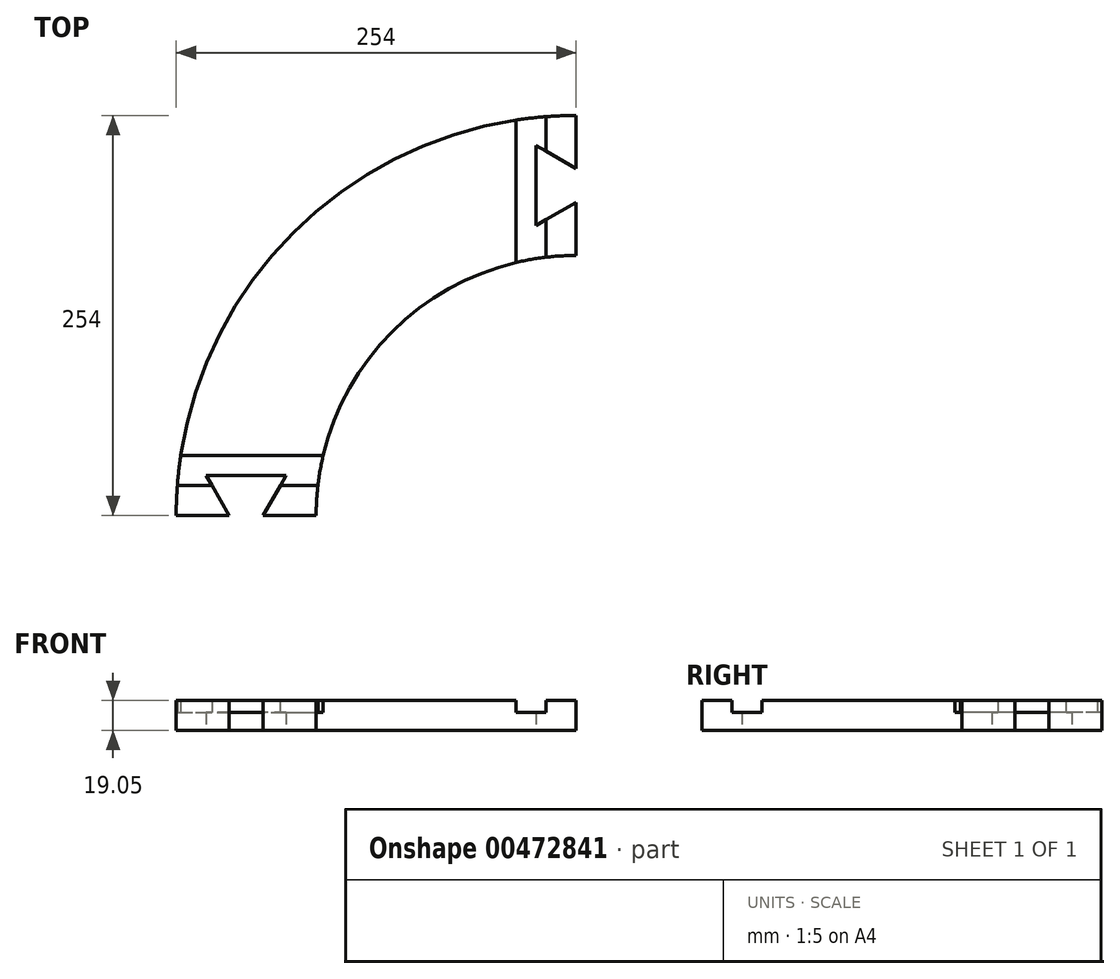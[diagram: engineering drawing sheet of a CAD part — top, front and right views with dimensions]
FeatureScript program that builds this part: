
annotation { "Feature Type Name" : "Feature", "Feature Type Description" : "" }
export const myFeature = defineFeature(function(context is Context, id is Id, definition is map)
    precondition{}
    {
        {
            var Q0;
            Q0=qCreatedBy(makeId("Top.planeOp"),FACE);
            var sketch = newSketch(context, id + "F0", { "sketchPlane" : qUnion([Q0])});
            skArc(sketch, "E0", {"start": v(-254, 0) * mm, "mid": v(-179.6, 179.6) * mm, "end": v(0, 254) * mm});
            skArc(sketch, "E1.0", {"start": v(-165.1, 0) * mm, "mid": v(-116.74, 116.74) * mm, "end": v(0, 165.1) * mm});
            skLineSegment(sketch, "E2", {"start": v(-254, 0) * mm, "end": v(-220.29, 0) * mm});
            skLineSegment(sketch, "E3", {"start": v(0, 254) * mm, "end": v(0, 220.29) * mm});
            skLineSegment(sketch, "E4", {"start": v(-220.29, 0) * mm, "end": v(-234.95, 25.4) * mm});
            skLineSegment(sketch, "E5", {"start": v(-234.95, 25.4) * mm, "end": v(-184.15, 25.4) * mm});
            skLineSegment(sketch, "E6", {"start": v(-184.15, 25.4) * mm, "end": v(-198.81, 0) * mm});
            skLineSegment(sketch, "E7.trimOffspring", {"start": v(-198.81, 0) * mm, "end": v(-165.1, 0) * mm});
            skLineSegment(sketch, "E8", {"start": v(0, 220.29) * mm, "end": v(-25.4, 234.95) * mm});
            skLineSegment(sketch, "E9", {"start": v(-25.4, 234.95) * mm, "end": v(-25.4, 184.15) * mm});
            skLineSegment(sketch, "E10", {"start": v(-25.4, 184.15) * mm, "end": v(0, 198.81) * mm});
            skLineSegment(sketch, "E11.trimOffspring", {"start": v(0, 198.81) * mm, "end": v(0, 165.1) * mm});
            skSolve(sketch);
        }
        {
            var Q0;
            Q0=qSketchRegion(id+"F0",true);
            extrude(context, id + "F1", {"entities" : qUnion([Q0]), "depth" : 19.05 * mm});
        }
        {
            var Q0;
            Q0=qCreatedBy(makeId("Right.planeOp"),FACE);
            var sketch = newSketch(context, id + "F2", { "sketchPlane" : qUnion([Q0])});
            skLineSegment(sketch, "E12.bottom", {"start": v(19.05, 11.43) * mm, "end": v(38.1, 11.43) * mm});
            skLineSegment(sketch, "E12.top", {"start": v(19.05, 19.05) * mm, "end": v(38.1, 19.05) * mm});
            skLineSegment(sketch, "E12.left", {"start": v(19.05, 11.43) * mm, "end": v(19.05, 19.05) * mm});
            skLineSegment(sketch, "E12.right", {"start": v(38.1, 11.43) * mm, "end": v(38.1, 19.05) * mm});
            skSolve(sketch);
        }
        {
            var Q0;
            Q0=qSketchRegion(id+"F2",true);
            extrude(context, id + "F3", {"entities" : qUnion([Q0]), "operationType" : NewBodyOperationType.REMOVE, "endBound" : BoundingType.THROUGH_ALL, "oppositeDirection" : true, "depth" : 25.4 * mm});
        }
        {
            var Q0;
            Q0=qCreatedBy(makeId("Front.planeOp"),FACE);
            var sketch = newSketch(context, id + "F4", { "sketchPlane" : qUnion([Q0])});
            skLineSegment(sketch, "E13.bottom", {"start": v(-19.05, 11.43) * mm, "end": v(-38.1, 11.43) * mm});
            skLineSegment(sketch, "E13.top", {"start": v(-19.05, 19.05) * mm, "end": v(-38.1, 19.05) * mm});
            skLineSegment(sketch, "E13.left", {"start": v(-19.05, 11.43) * mm, "end": v(-19.05, 19.05) * mm});
            skLineSegment(sketch, "E13.right", {"start": v(-38.1, 11.43) * mm, "end": v(-38.1, 19.05) * mm});
            skSolve(sketch);
        }
        {
            var Q0;
            Q0=qSketchRegion(id+"F4",true);
            extrude(context, id + "F5", {"entities" : qUnion([Q0]), "operationType" : NewBodyOperationType.REMOVE, "endBound" : BoundingType.THROUGH_ALL, "oppositeDirection" : true, "depth" : 25.4 * mm});
        }
    });
